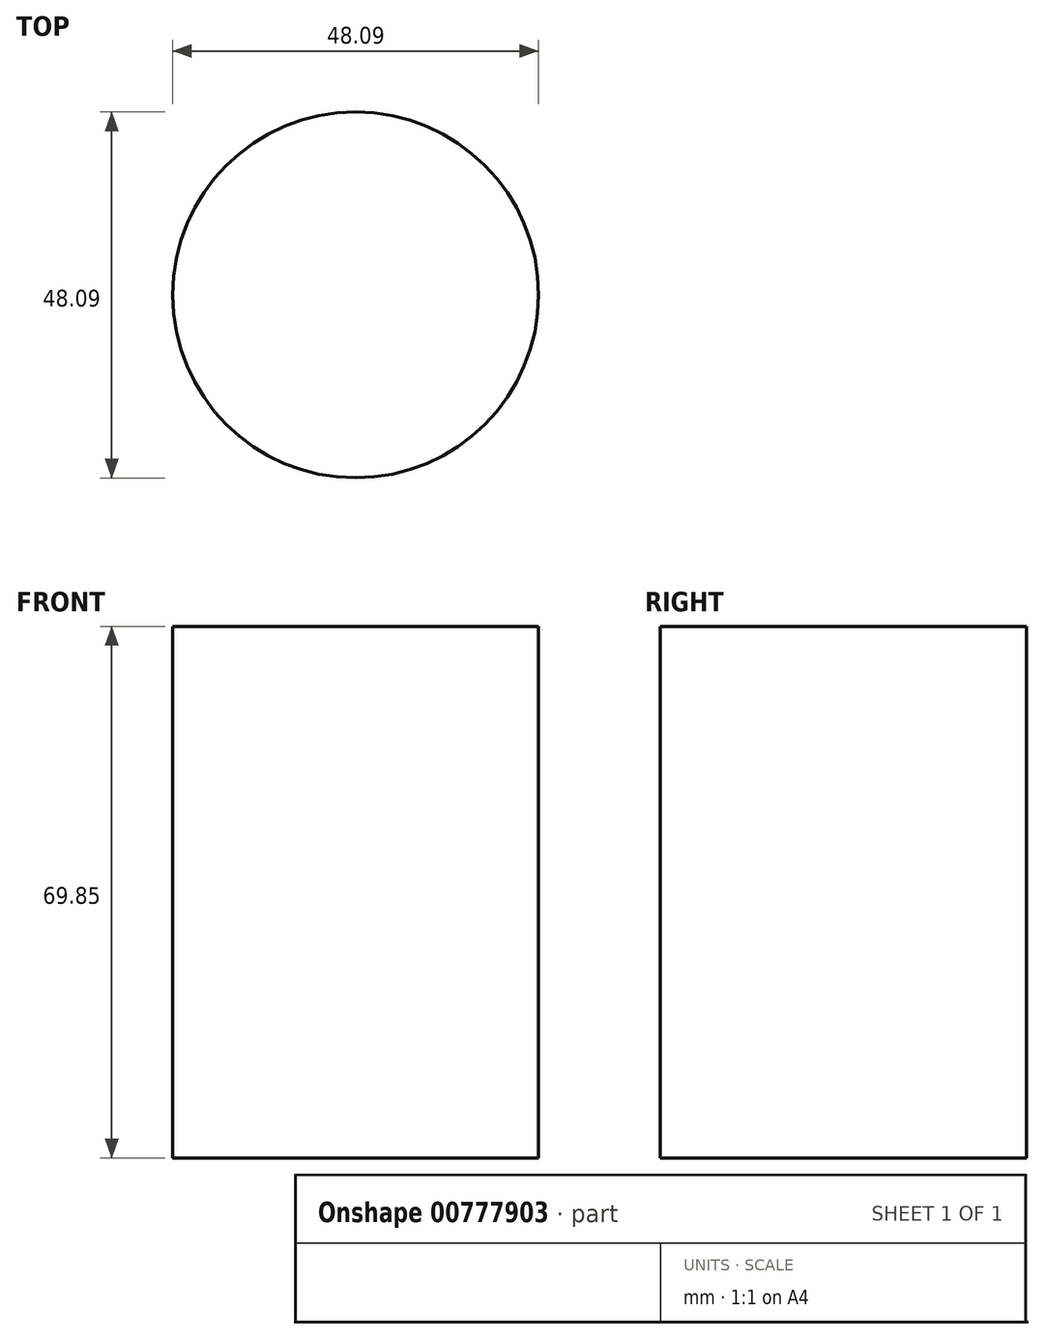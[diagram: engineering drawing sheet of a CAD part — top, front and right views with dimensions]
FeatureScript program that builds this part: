
annotation { "Feature Type Name" : "Feature", "Feature Type Description" : "" }
export const myFeature = defineFeature(function(context is Context, id is Id, definition is map)
    precondition{}
    {
        {
            var Q0;
            Q0=qCreatedBy(makeId("Top.planeOp"),FACE);
            var sketch = newSketch(context, id + "F0", { "sketchPlane" : qUnion([Q0])});
            skCircle(sketch, "E0", {"center": v(26.35, 42.04) * mm, "radius": 24.04 * mm});
            skSolve(sketch);
        }
        {
            var Q0;
            Q0=makeQuery(id+"F0.imprint","IMPRINT",FACE,{"disambiguationData":[TD([[makeQuery(id+"F0.imprint","IMPRINT",EDGE,{"derivedFrom":sQuery(id+"F0.wireOp",EDGE,"E0")}),1.0]])]});
            extrude(context, id + "F1", {"entities" : qUnion([Q0]), "depth" : 69.85 * mm, "offsetDistance" : 25.4 * mm});
        }
    });
